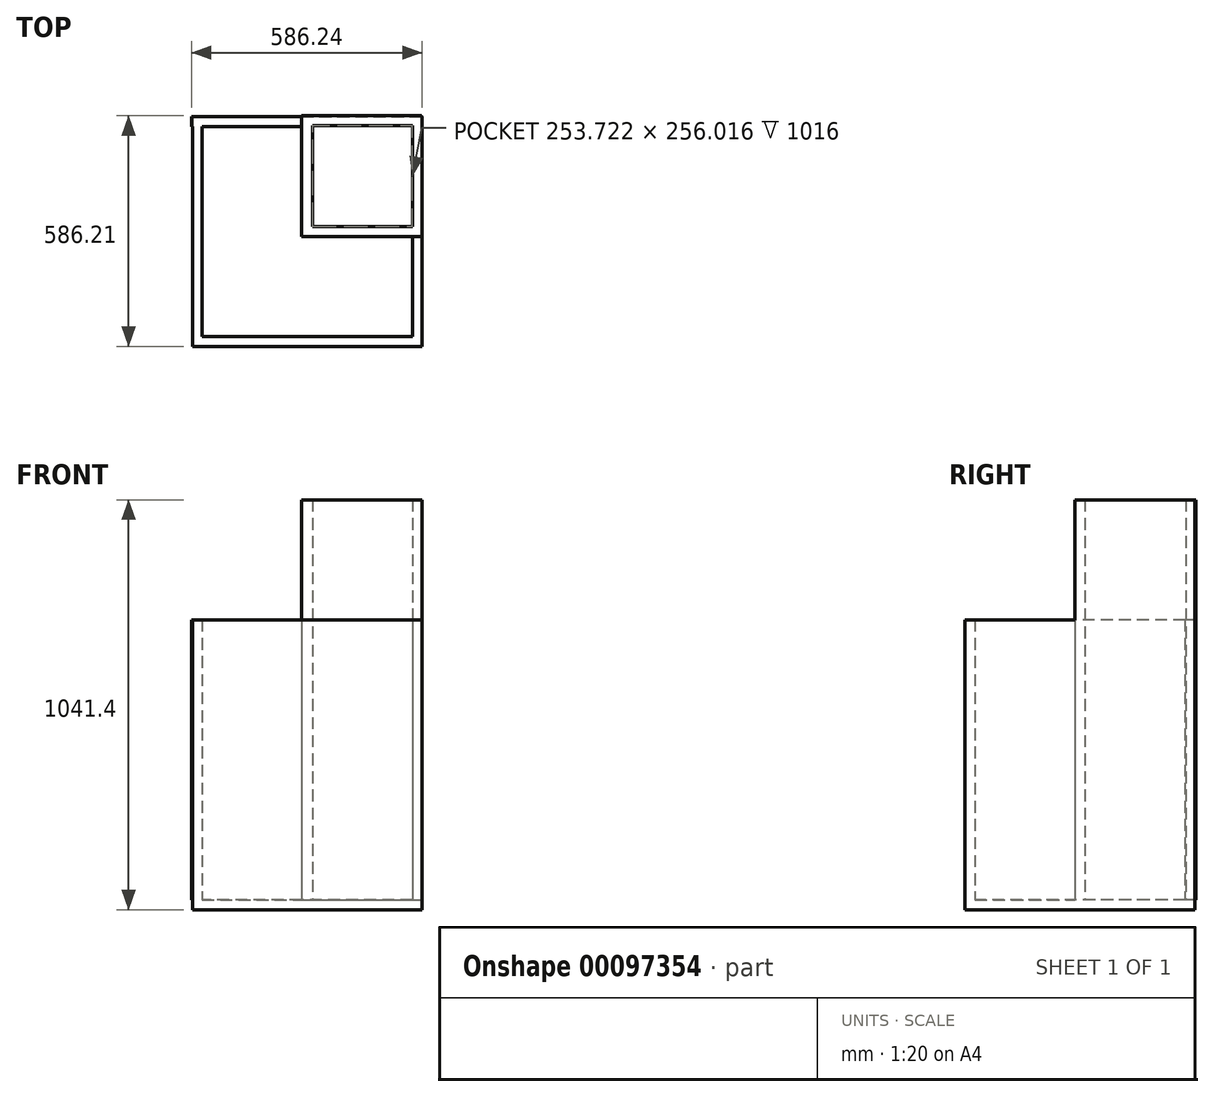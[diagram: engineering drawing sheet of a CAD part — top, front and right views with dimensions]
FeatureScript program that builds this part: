
annotation { "Feature Type Name" : "Feature", "Feature Type Description" : "" }
export const myFeature = defineFeature(function(context is Context, id is Id, definition is map)
    precondition{}
    {
        {
            var Q0;
            Q0=qCreatedBy(makeId("Top.planeOp"),FACE);
            var sketch = newSketch(context, id + "F0", { "sketchPlane" : qUnion([Q0])});
            skLineSegment(sketch, "E0.bottom", {"start": v(-305.08, 360.03) * mm, "end": v(279.12, 360.03) * mm});
            skLineSegment(sketch, "E0.top", {"start": v(-305.08, -224.17) * mm, "end": v(279.12, -224.17) * mm});
            skLineSegment(sketch, "E0.left", {"start": v(-305.08, 360.03) * mm, "end": v(-305.08, -224.17) * mm});
            skLineSegment(sketch, "E0.right", {"start": v(279.12, 360.03) * mm, "end": v(279.12, -224.17) * mm});
            skSolve(sketch);
        }
        {
            var Q0;
            Q0=makeQuery(id+"F0.imprint","IMPRINT",FACE,{"disambiguationData":[TD([[makeQuery(id+"F0.imprint","IMPRINT",EDGE,{"derivedFrom":sQuery(id+"F0.wireOp",EDGE,"E0.bottom")}),-1.0]])]});
            extrude(context, id + "F1", {"entities" : qUnion([Q0]), "depth" : 25.4 * mm});
        }
        {
            var Q0;
            Q0=makeQuery(id+"F1.opExtrude","CAP_FACE",FACE,{"disambiguationData":[OSD([sQuery(id+"F0.wireOp",EDGE,"E0.bottom"),sQuery(id+"F0.wireOp",EDGE,"E0.top"),sQuery(id+"F0.wireOp",EDGE,"E0.left"),sQuery(id+"F0.wireOp",EDGE,"E0.right")])],"isStart":false});
            var sketch = newSketch(context, id + "F2", { "sketchPlane" : qUnion([Q0])});
            skLineSegment(sketch, "E1.bottom", {"start": v(279.12, 360.03) * mm, "end": v(253.72, 360.03) * mm});
            skLineSegment(sketch, "E1.top", {"start": v(279.12, 55.23) * mm, "end": v(253.72, 55.23) * mm});
            skLineSegment(sketch, "E1.left", {"start": v(279.12, 360.03) * mm, "end": v(279.12, 55.23) * mm});
            skLineSegment(sketch, "E1.right", {"start": v(253.72, 360.03) * mm, "end": v(253.72, 55.23) * mm});
            skSolve(sketch);
        }
        {
            var Q0;
            Q0 = qSketchRegion(id + "F2", true);
            extrude(context, id + "F3", {"entities" : qUnion([Q0]), "operationType" : NewBodyOperationType.ADD, "depth" : 1016 * mm});
        }
        {
            var Q0;
            Q0=makeQuery(id+"F1.opExtrude","CAP_FACE",FACE,{"disambiguationData":[OSD([sQuery(id+"F0.wireOp",EDGE,"E0.bottom"),sQuery(id+"F0.wireOp",EDGE,"E0.top"),sQuery(id+"F0.wireOp",EDGE,"E0.left"),sQuery(id+"F0.wireOp",EDGE,"E0.right")])],"isStart":false});
            var sketch = newSketch(context, id + "F4", { "sketchPlane" : qUnion([Q0])});
            skLineSegment(sketch, "E2.bottom", {"start": v(277.08, 362.04) * mm, "end": v(-27.72, 362.04) * mm});
            skLineSegment(sketch, "E2.top", {"start": v(277.08, 336.64) * mm, "end": v(-27.72, 336.64) * mm});
            skLineSegment(sketch, "E2.left", {"start": v(277.08, 362.04) * mm, "end": v(277.08, 336.64) * mm});
            skLineSegment(sketch, "E2.right", {"start": v(-27.72, 362.04) * mm, "end": v(-27.72, 336.64) * mm});
            skSolve(sketch);
        }
        {
            var Q0;
            Q0 = qSketchRegion(id + "F4", true);
            extrude(context, id + "F5", {"entities" : qUnion([Q0]), "operationType" : NewBodyOperationType.ADD, "depth" : 1016 * mm});
        }
        {
            var Q0;
            Q0=makeQuery(id+"F1.opExtrude","CAP_FACE",FACE,{"disambiguationData":[OSD([sQuery(id+"F0.wireOp",EDGE,"E0.bottom"),sQuery(id+"F0.wireOp",EDGE,"E0.top"),sQuery(id+"F0.wireOp",EDGE,"E0.left"),sQuery(id+"F0.wireOp",EDGE,"E0.right")])],"isStart":false});
            var sketch = newSketch(context, id + "F6", { "sketchPlane" : qUnion([Q0])});
            skLineSegment(sketch, "E3.bottom", {"start": v(-27.72, 360.03) * mm, "end": v(0, 360.03) * mm});
            skLineSegment(sketch, "E3.top", {"start": v(-27.72, 55.23) * mm, "end": v(0, 55.23) * mm});
            skLineSegment(sketch, "E3.left", {"start": v(-27.72, 360.03) * mm, "end": v(-27.72, 55.23) * mm});
            skLineSegment(sketch, "E3.right", {"start": v(0, 360.03) * mm, "end": v(0, 55.23) * mm});
            skSolve(sketch);
        }
        {
            var Q0;
            Q0 = qSketchRegion(id + "F6", true);
            extrude(context, id + "F7", {"entities" : qUnion([Q0]), "operationType" : NewBodyOperationType.ADD, "depth" : 1016 * mm});
        }
        {
            var Q0;
            Q0=makeQuery(id+"F1.opExtrude","CAP_FACE",FACE,{"disambiguationData":[OSD([sQuery(id+"F0.wireOp",EDGE,"E0.bottom"),sQuery(id+"F0.wireOp",EDGE,"E0.top"),sQuery(id+"F0.wireOp",EDGE,"E0.left"),sQuery(id+"F0.wireOp",EDGE,"E0.right")])],"isStart":false});
            var sketch = newSketch(context, id + "F8", { "sketchPlane" : qUnion([Q0])});
            skLineSegment(sketch, "E4.bottom", {"start": v(279.12, 55.23) * mm, "end": v(-27.72, 55.23) * mm});
            skLineSegment(sketch, "E4.top", {"start": v(279.12, 80.63) * mm, "end": v(-27.72, 80.63) * mm});
            skLineSegment(sketch, "E4.left", {"start": v(279.12, 55.23) * mm, "end": v(279.12, 80.63) * mm});
            skLineSegment(sketch, "E4.right", {"start": v(-27.72, 55.23) * mm, "end": v(-27.72, 80.63) * mm});
            skSolve(sketch);
        }
        {
            var Q0;
            Q0 = qSketchRegion(id + "F8", true);
            extrude(context, id + "F9", {"entities" : qUnion([Q0]), "operationType" : NewBodyOperationType.ADD, "depth" : 1016 * mm});
        }
        {
            var Q0;
            {var subQ1=sQuery(id+"F0.wireOp",EDGE,"E0.left");var subQ2=sQuery(id+"F0.wireOp",EDGE,"E0.bottom");var subQ3=sQuery(id+"F0.wireOp",EDGE,"E0.top");var subQ4=sQuery(id+"F0.wireOp",EDGE,"E0.right");Q0=makeQuery(id+"F9.boolean.opBoolean","SPLIT",FACE,{"disambiguationData":[TD([makeQuery(id+"F1.opExtrude","SWEPT_FACE",FACE,{"disambiguationData":[OSD([subQ2])]})])],"derivedFrom":makeQuery(id+"F1.opExtrude","CAP_FACE",FACE,{"disambiguationData":[OSD([subQ2,subQ3,subQ1,subQ4])],"isStart":false})});}
            var sketch = newSketch(context, id + "F10", { "sketchPlane" : qUnion([Q0])});
            skLineSegment(sketch, "E5.bottom", {"start": v(279.12, -224.17) * mm, "end": v(253.72, -224.17) * mm});
            skLineSegment(sketch, "E5.top", {"start": v(279.12, 55.23) * mm, "end": v(253.72, 55.23) * mm});
            skLineSegment(sketch, "E5.left", {"start": v(279.12, -224.17) * mm, "end": v(279.12, 55.23) * mm});
            skLineSegment(sketch, "E5.right", {"start": v(253.72, -224.17) * mm, "end": v(253.72, 55.23) * mm});
            skSolve(sketch);
        }
        {
            var Q0;
            Q0 = qSketchRegion(id + "F10", true);
            extrude(context, id + "F11", {"entities" : qUnion([Q0]), "operationType" : NewBodyOperationType.ADD, "depth" : 711.2 * mm});
        }
        {
            var Q0;
            {var subQ1=sQuery(id+"F0.wireOp",EDGE,"E0.left");var subQ2=sQuery(id+"F0.wireOp",EDGE,"E0.bottom");var subQ3=sQuery(id+"F0.wireOp",EDGE,"E0.top");var subQ4=sQuery(id+"F0.wireOp",EDGE,"E0.right");Q0=makeQuery(id+"F9.boolean.opBoolean","SPLIT",FACE,{"disambiguationData":[TD([makeQuery(id+"F1.opExtrude","SWEPT_FACE",FACE,{"disambiguationData":[OSD([subQ2])]})])],"derivedFrom":makeQuery(id+"F1.opExtrude","CAP_FACE",FACE,{"disambiguationData":[OSD([subQ2,subQ3,subQ1,subQ4])],"isStart":false})});}
            var sketch = newSketch(context, id + "F12", { "sketchPlane" : qUnion([Q0])});
            skLineSegment(sketch, "E6.bottom", {"start": v(-305.08, -224.17) * mm, "end": v(279.12, -224.17) * mm});
            skLineSegment(sketch, "E6.top", {"start": v(-305.08, -198.77) * mm, "end": v(279.12, -198.77) * mm});
            skLineSegment(sketch, "E6.left", {"start": v(-305.08, -224.17) * mm, "end": v(-305.08, -198.77) * mm});
            skLineSegment(sketch, "E6.right", {"start": v(279.12, -224.17) * mm, "end": v(279.12, -198.77) * mm});
            skSolve(sketch);
        }
        {
            var Q0;
            Q0 = qSketchRegion(id + "F12", true);
            extrude(context, id + "F13", {"entities" : qUnion([Q0]), "operationType" : NewBodyOperationType.ADD, "depth" : 711.2 * mm});
        }
        {
            var Q0;
            {var subQ1=sQuery(id+"F0.wireOp",EDGE,"E0.left");var subQ2=sQuery(id+"F0.wireOp",EDGE,"E0.bottom");var subQ3=sQuery(id+"F0.wireOp",EDGE,"E0.top");var subQ4=sQuery(id+"F0.wireOp",EDGE,"E0.right");Q0=makeQuery(id+"F9.boolean.opBoolean","SPLIT",FACE,{"disambiguationData":[TD([makeQuery(id+"F1.opExtrude","SWEPT_FACE",FACE,{"disambiguationData":[OSD([subQ2])]})])],"derivedFrom":makeQuery(id+"F1.opExtrude","CAP_FACE",FACE,{"disambiguationData":[OSD([subQ2,subQ3,subQ1,subQ4])],"isStart":false})});}
            var sketch = newSketch(context, id + "F14", { "sketchPlane" : qUnion([Q0])});
            skLineSegment(sketch, "E7.bottom", {"start": v(-305.08, 360.03) * mm, "end": v(-279.68, 360.03) * mm});
            skLineSegment(sketch, "E7.top", {"start": v(-305.08, -224.17) * mm, "end": v(-279.68, -224.17) * mm});
            skLineSegment(sketch, "E7.left", {"start": v(-305.08, 360.03) * mm, "end": v(-305.08, -224.17) * mm});
            skLineSegment(sketch, "E7.right", {"start": v(-279.68, 360.03) * mm, "end": v(-279.68, -224.17) * mm});
            skSolve(sketch);
        }
        {
            var Q0;
            Q0 = qSketchRegion(id + "F14", true);
            extrude(context, id + "F15", {"entities" : qUnion([Q0]), "operationType" : NewBodyOperationType.ADD, "depth" : 711.2 * mm});
        }
        {
            var Q0;
            {var subQ1=sQuery(id+"F0.wireOp",EDGE,"E0.left");var subQ2=sQuery(id+"F0.wireOp",EDGE,"E0.bottom");var subQ3=sQuery(id+"F0.wireOp",EDGE,"E0.top");var subQ4=sQuery(id+"F0.wireOp",EDGE,"E0.right");Q0=makeQuery(id+"F9.boolean.opBoolean","SPLIT",FACE,{"disambiguationData":[TD([makeQuery(id+"F1.opExtrude","SWEPT_FACE",FACE,{"disambiguationData":[OSD([subQ2])]})])],"derivedFrom":makeQuery(id+"F1.opExtrude","CAP_FACE",FACE,{"disambiguationData":[OSD([subQ2,subQ3,subQ1,subQ4])],"isStart":false})});}
            var sketch = newSketch(context, id + "F16", { "sketchPlane" : qUnion([Q0])});
            skLineSegment(sketch, "E8.bottom", {"start": v(-27.72, 334.63) * mm, "end": v(-307.12, 334.63) * mm});
            skLineSegment(sketch, "E8.top", {"start": v(-27.72, 360.03) * mm, "end": v(-307.12, 360.03) * mm});
            skLineSegment(sketch, "E8.left", {"start": v(-27.72, 334.63) * mm, "end": v(-27.72, 360.03) * mm});
            skLineSegment(sketch, "E8.right", {"start": v(-307.12, 334.63) * mm, "end": v(-307.12, 360.03) * mm});
            skSolve(sketch);
        }
        {
            var Q0;
            Q0 = qSketchRegion(id + "F16", true);
            extrude(context, id + "F17", {"entities" : qUnion([Q0]), "operationType" : NewBodyOperationType.ADD, "depth" : 711.2 * mm});
        }
    });
